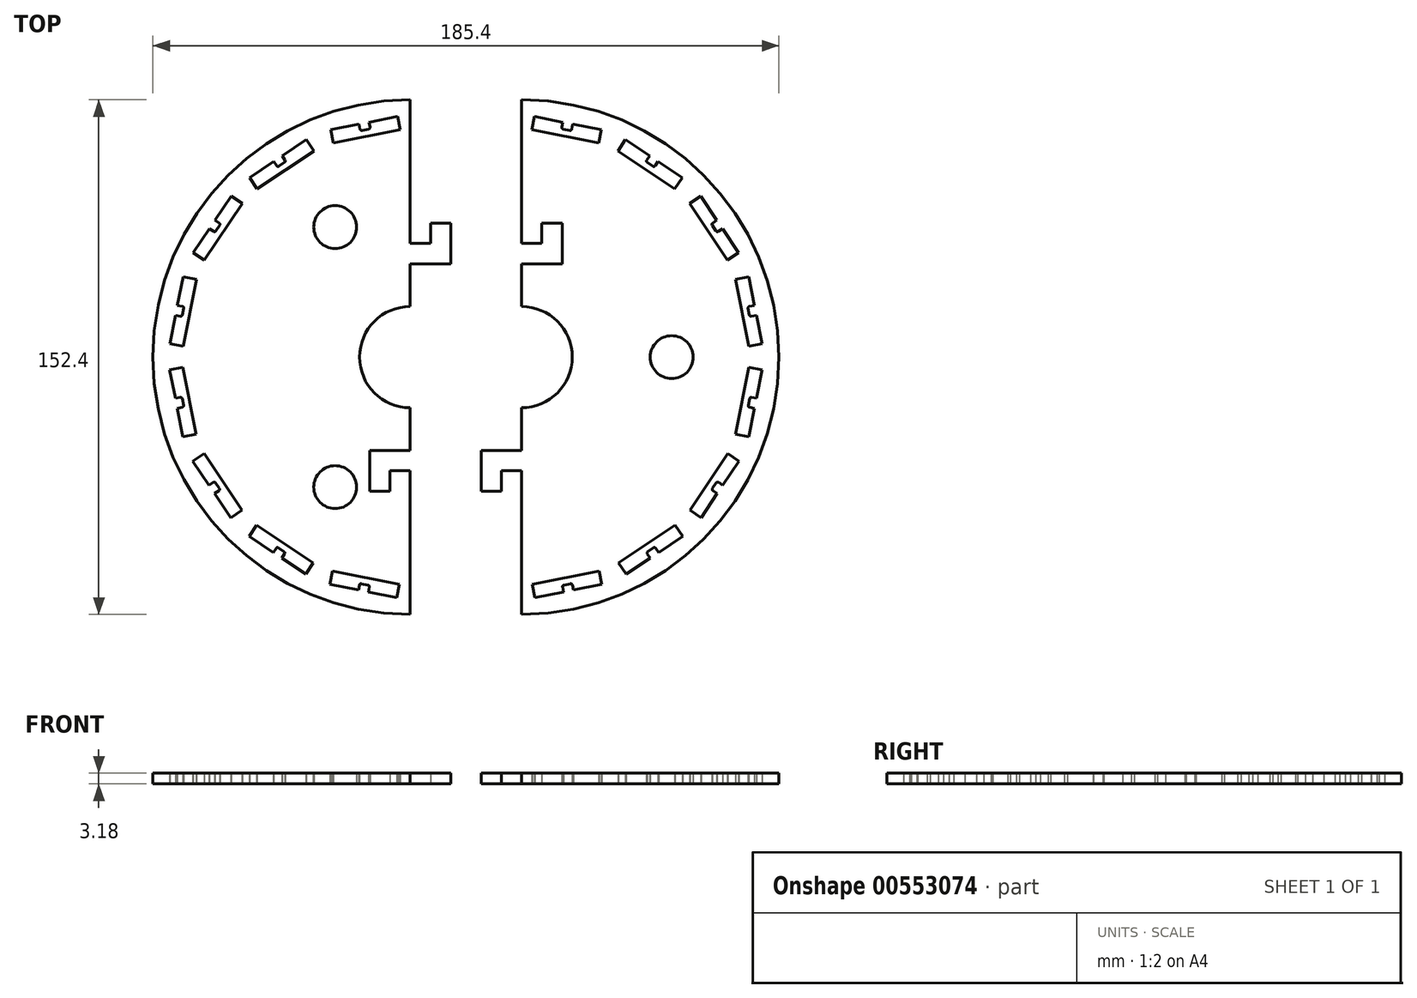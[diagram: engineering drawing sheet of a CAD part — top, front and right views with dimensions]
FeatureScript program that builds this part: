
annotation { "Feature Type Name" : "Feature", "Feature Type Description" : "" }
export const myFeature = defineFeature(function(context is Context, id is Id, definition is map)
    precondition{}
    {
        {
            var Q0;
            Q0=qCreatedBy(makeId("Top.planeOp"),FACE);
            var sketch = newSketch(context, id + "F0", { "sketchPlane" : qUnion([Q0])});
            skLineSegment(sketch, "E0.8.0", {"start": v(23, -63.34) * mm, "end": v(23.78, -67.27) * mm});
            skPoint(sketch, "E0.8.1", {"position": v(14.95, -66.98) * mm});
            skPoint(sketch, "E0.8.2", {"position": v(12.01, -67.57) * mm});
            skLineSegment(sketch, "E0.8.3", {"start": v(23, -63.34) * mm, "end": v(3.19, -67.28) * mm});
            skLineSegment(sketch, "E0.8.4", {"start": v(3.97, -71.2) * mm, "end": v(3.19, -67.28) * mm});
            skLineSegment(sketch, "E0.8.5", {"start": v(12.4, -69.53) * mm, "end": v(3.97, -71.2) * mm});
            skLineSegment(sketch, "E0.8.6", {"start": v(23.78, -67.27) * mm, "end": v(15.34, -68.94) * mm});
            skLineSegment(sketch, "E0.8.7", {"start": v(12.1, -68.06) * mm, "end": v(12.4, -69.53) * mm});
            skArc(sketch, "E0.8.8", {"start": v(15.05, -67.47) * mm, "mid": v(14.84, -67.15) * mm, "end": v(14.46, -67.08) * mm});
            skLineSegment(sketch, "E0.8.9", {"start": v(15.05, -67.47) * mm, "end": v(15.34, -68.94) * mm});
            skArc(sketch, "E0.8.10", {"start": v(12.5, -67.47) * mm, "mid": v(12.18, -67.68) * mm, "end": v(12.1, -68.06) * mm});
            skLineSegment(sketch, "E0.8.11", {"start": v(14.46, -67.08) * mm, "end": v(12.5, -67.47) * mm});
            skLineSegment(sketch, "E0.9.0", {"start": v(45.48, -49.72) * mm, "end": v(47.7, -53.05) * mm});
            skPoint(sketch, "E0.9.1", {"position": v(39.45, -56.16) * mm});
            skPoint(sketch, "E0.9.2", {"position": v(36.95, -57.83) * mm});
            skLineSegment(sketch, "E0.9.3", {"start": v(45.48, -49.72) * mm, "end": v(28.7, -60.94) * mm});
            skLineSegment(sketch, "E0.9.4", {"start": v(30.92, -64.27) * mm, "end": v(28.7, -60.94) * mm});
            skLineSegment(sketch, "E0.9.5", {"start": v(38.06, -59.5) * mm, "end": v(30.92, -64.27) * mm});
            skLineSegment(sketch, "E0.9.6", {"start": v(47.7, -53.05) * mm, "end": v(40.56, -57.82) * mm});
            skLineSegment(sketch, "E0.9.7", {"start": v(37.23, -58.24) * mm, "end": v(38.06, -59.5) * mm});
            skArc(sketch, "E0.9.8", {"start": v(39.73, -56.58) * mm, "mid": v(39.4, -56.36) * mm, "end": v(39.03, -56.44) * mm});
            skLineSegment(sketch, "E0.9.9", {"start": v(39.73, -56.58) * mm, "end": v(40.56, -57.82) * mm});
            skArc(sketch, "E0.9.10", {"start": v(37.37, -57.55) * mm, "mid": v(37.16, -57.87) * mm, "end": v(37.23, -58.24) * mm});
            skLineSegment(sketch, "E0.9.11", {"start": v(39.03, -56.44) * mm, "end": v(37.37, -57.55) * mm});
            skLineSegment(sketch, "E0.10.0", {"start": v(61.05, -28.53) * mm, "end": v(64.38, -30.75) * mm});
            skPoint(sketch, "E0.10.1", {"position": v(57.94, -36.8) * mm});
            skPoint(sketch, "E0.10.2", {"position": v(56.27, -39.28) * mm});
            skLineSegment(sketch, "E0.10.3", {"start": v(61.05, -28.53) * mm, "end": v(49.83, -45.32) * mm});
            skLineSegment(sketch, "E0.10.4", {"start": v(53.16, -47.54) * mm, "end": v(49.83, -45.32) * mm});
            skLineSegment(sketch, "E0.10.5", {"start": v(57.93, -40.4) * mm, "end": v(53.16, -47.54) * mm});
            skLineSegment(sketch, "E0.10.6", {"start": v(64.38, -30.75) * mm, "end": v(59.6, -37.9) * mm});
            skLineSegment(sketch, "E0.10.7", {"start": v(56.69, -39.56) * mm, "end": v(57.93, -40.4) * mm});
            skArc(sketch, "E0.10.8", {"start": v(58.35, -37.07) * mm, "mid": v(57.98, -37) * mm, "end": v(57.66, -37.2) * mm});
            skLineSegment(sketch, "E0.10.9", {"start": v(58.35, -37.07) * mm, "end": v(59.6, -37.9) * mm});
            skArc(sketch, "E0.10.10", {"start": v(56.55, -38.87) * mm, "mid": v(56.47, -39.24) * mm, "end": v(56.69, -39.56) * mm});
            skLineSegment(sketch, "E0.10.11", {"start": v(57.66, -37.2) * mm, "end": v(56.55, -38.87) * mm});
            skLineSegment(sketch, "E0.11.0", {"start": v(67.32, -3) * mm, "end": v(71.24, -3.78) * mm});
            skPoint(sketch, "E0.11.1", {"position": v(67.6, -11.82) * mm});
            skPoint(sketch, "E0.11.2", {"position": v(67.02, -14.76) * mm});
            skLineSegment(sketch, "E0.11.3", {"start": v(67.32, -3) * mm, "end": v(63.38, -22.8) * mm});
            skLineSegment(sketch, "E0.11.4", {"start": v(67.3, -23.58) * mm, "end": v(63.38, -22.8) * mm});
            skLineSegment(sketch, "E0.11.5", {"start": v(68.98, -15.15) * mm, "end": v(67.3, -23.58) * mm});
            skLineSegment(sketch, "E0.11.6", {"start": v(71.24, -3.78) * mm, "end": v(69.57, -12.2) * mm});
            skLineSegment(sketch, "E0.11.7", {"start": v(67.51, -14.86) * mm, "end": v(68.98, -15.15) * mm});
            skArc(sketch, "E0.11.8", {"start": v(68.1, -11.92) * mm, "mid": v(67.72, -12) * mm, "end": v(67.5, -12.3) * mm});
            skLineSegment(sketch, "E0.11.9", {"start": v(68.1, -11.92) * mm, "end": v(69.57, -12.2) * mm});
            skArc(sketch, "E0.11.10", {"start": v(67.12, -14.27) * mm, "mid": v(67.2, -14.65) * mm, "end": v(67.51, -14.86) * mm});
            skLineSegment(sketch, "E0.11.11", {"start": v(67.5, -12.3) * mm, "end": v(67.12, -14.27) * mm});
            skLineSegment(sketch, "E0.12.0", {"start": v(63.34, 23) * mm, "end": v(67.27, 23.78) * mm});
            skPoint(sketch, "E0.12.1", {"position": v(66.98, 14.95) * mm});
            skPoint(sketch, "E0.12.2", {"position": v(67.57, 12.01) * mm});
            skLineSegment(sketch, "E0.12.3", {"start": v(63.34, 23) * mm, "end": v(67.28, 3.19) * mm});
            skLineSegment(sketch, "E0.12.4", {"start": v(71.2, 3.97) * mm, "end": v(67.28, 3.19) * mm});
            skLineSegment(sketch, "E0.12.5", {"start": v(69.53, 12.4) * mm, "end": v(71.2, 3.97) * mm});
            skLineSegment(sketch, "E0.12.6", {"start": v(67.27, 23.78) * mm, "end": v(68.94, 15.34) * mm});
            skLineSegment(sketch, "E0.12.7", {"start": v(68.06, 12.1) * mm, "end": v(69.53, 12.4) * mm});
            skArc(sketch, "E0.12.8", {"start": v(67.47, 15.05) * mm, "mid": v(67.15, 14.84) * mm, "end": v(67.08, 14.46) * mm});
            skLineSegment(sketch, "E0.12.9", {"start": v(67.47, 15.05) * mm, "end": v(68.94, 15.34) * mm});
            skArc(sketch, "E0.12.10", {"start": v(67.47, 12.5) * mm, "mid": v(67.68, 12.18) * mm, "end": v(68.06, 12.1) * mm});
            skLineSegment(sketch, "E0.12.11", {"start": v(67.08, 14.46) * mm, "end": v(67.47, 12.5) * mm});
            skLineSegment(sketch, "E0.13.0", {"start": v(49.72, 45.48) * mm, "end": v(53.05, 47.7) * mm});
            skPoint(sketch, "E0.13.1", {"position": v(56.16, 39.45) * mm});
            skPoint(sketch, "E0.13.2", {"position": v(57.83, 36.95) * mm});
            skLineSegment(sketch, "E0.13.3", {"start": v(49.72, 45.48) * mm, "end": v(60.94, 28.7) * mm});
            skLineSegment(sketch, "E0.13.4", {"start": v(64.27, 30.92) * mm, "end": v(60.94, 28.7) * mm});
            skLineSegment(sketch, "E0.13.5", {"start": v(59.5, 38.06) * mm, "end": v(64.27, 30.92) * mm});
            skLineSegment(sketch, "E0.13.6", {"start": v(53.05, 47.7) * mm, "end": v(57.82, 40.56) * mm});
            skLineSegment(sketch, "E0.13.7", {"start": v(58.24, 37.23) * mm, "end": v(59.5, 38.06) * mm});
            skArc(sketch, "E0.13.8", {"start": v(56.58, 39.73) * mm, "mid": v(56.36, 39.4) * mm, "end": v(56.44, 39.03) * mm});
            skLineSegment(sketch, "E0.13.9", {"start": v(56.58, 39.73) * mm, "end": v(57.82, 40.56) * mm});
            skArc(sketch, "E0.13.10", {"start": v(57.55, 37.37) * mm, "mid": v(57.87, 37.16) * mm, "end": v(58.24, 37.23) * mm});
            skLineSegment(sketch, "E0.13.11", {"start": v(56.44, 39.03) * mm, "end": v(57.55, 37.37) * mm});
            skLineSegment(sketch, "E0.14.0", {"start": v(28.53, 61.05) * mm, "end": v(30.75, 64.38) * mm});
            skPoint(sketch, "E0.14.1", {"position": v(36.8, 57.94) * mm});
            skPoint(sketch, "E0.14.2", {"position": v(39.28, 56.27) * mm});
            skLineSegment(sketch, "E0.14.3", {"start": v(28.53, 61.05) * mm, "end": v(45.32, 49.83) * mm});
            skLineSegment(sketch, "E0.14.4", {"start": v(47.54, 53.16) * mm, "end": v(45.32, 49.83) * mm});
            skLineSegment(sketch, "E0.14.5", {"start": v(40.4, 57.93) * mm, "end": v(47.54, 53.16) * mm});
            skLineSegment(sketch, "E0.14.6", {"start": v(30.75, 64.38) * mm, "end": v(37.9, 59.6) * mm});
            skLineSegment(sketch, "E0.14.7", {"start": v(39.56, 56.69) * mm, "end": v(40.4, 57.93) * mm});
            skArc(sketch, "E0.14.8", {"start": v(37.07, 58.35) * mm, "mid": v(37, 57.98) * mm, "end": v(37.2, 57.66) * mm});
            skLineSegment(sketch, "E0.14.9", {"start": v(37.07, 58.35) * mm, "end": v(37.9, 59.6) * mm});
            skArc(sketch, "E0.14.10", {"start": v(38.87, 56.55) * mm, "mid": v(39.24, 56.47) * mm, "end": v(39.56, 56.69) * mm});
            skLineSegment(sketch, "E0.14.11", {"start": v(37.2, 57.66) * mm, "end": v(38.87, 56.55) * mm});
            skLineSegment(sketch, "E0.15.0", {"start": v(3, 67.32) * mm, "end": v(3.78, 71.24) * mm});
            skPoint(sketch, "E0.15.1", {"position": v(11.82, 67.6) * mm});
            skPoint(sketch, "E0.15.2", {"position": v(14.76, 67.02) * mm});
            skLineSegment(sketch, "E0.15.3", {"start": v(3, 67.32) * mm, "end": v(22.8, 63.38) * mm});
            skLineSegment(sketch, "E0.15.4", {"start": v(23.58, 67.3) * mm, "end": v(22.8, 63.38) * mm});
            skLineSegment(sketch, "E0.15.5", {"start": v(15.15, 68.98) * mm, "end": v(23.58, 67.3) * mm});
            skLineSegment(sketch, "E0.15.6", {"start": v(3.78, 71.24) * mm, "end": v(12.2, 69.57) * mm});
            skLineSegment(sketch, "E0.15.7", {"start": v(14.86, 67.51) * mm, "end": v(15.15, 68.98) * mm});
            skArc(sketch, "E0.15.8", {"start": v(11.92, 68.1) * mm, "mid": v(12, 67.72) * mm, "end": v(12.3, 67.5) * mm});
            skLineSegment(sketch, "E0.15.9", {"start": v(11.92, 68.1) * mm, "end": v(12.2, 69.57) * mm});
            skArc(sketch, "E0.15.10", {"start": v(14.27, 67.12) * mm, "mid": v(14.65, 67.2) * mm, "end": v(14.86, 67.51) * mm});
            skLineSegment(sketch, "E0.15.11", {"start": v(12.3, 67.5) * mm, "end": v(14.27, 67.12) * mm});
            skPoint(sketch, "E0.center", {"position": v(0, 0) * mm});
            skArc(sketch, "E1", {"start": v(0, -76.2) * mm, "mid": v(76.2, 0) * mm, "end": v(0, 76.2) * mm});
            skArc(sketch, "E2", {"start": v(0, -15) * mm, "mid": v(15, 0) * mm, "end": v(0, 15) * mm});
            skLineSegment(sketch, "E3", {"start": v(0, 33.66) * mm, "end": v(6, 33.66) * mm});
            skLineSegment(sketch, "E4", {"start": v(6, 33.66) * mm, "end": v(6, 39.66) * mm});
            skLineSegment(sketch, "E5", {"start": v(6, 39.66) * mm, "end": v(12, 39.66) * mm});
            skLineSegment(sketch, "E6", {"start": v(12, 39.66) * mm, "end": v(12, 27.66) * mm});
            skLineSegment(sketch, "E7", {"start": v(12, 27.66) * mm, "end": v(0, 27.66) * mm});
            skLineSegment(sketch, "E8.1.0", {"start": v(-12, -27.66) * mm, "end": v(0, -27.66) * mm});
            skLineSegment(sketch, "E8.1.1", {"start": v(-6, -39.66) * mm, "end": v(-12, -39.66) * mm});
            skLineSegment(sketch, "E8.1.2", {"start": v(0, -33.66) * mm, "end": v(-6, -33.66) * mm});
            skLineSegment(sketch, "E8.1.3", {"start": v(-6, -33.66) * mm, "end": v(-6, -39.66) * mm});
            skLineSegment(sketch, "E8.1.4", {"start": v(-12, -39.66) * mm, "end": v(-12, -27.66) * mm});
            skLineSegment(sketch, "E9", {"start": v(0, -27.66) * mm, "end": v(0, -15) * mm});
            skLineSegment(sketch, "E10", {"start": v(0, 15) * mm, "end": v(0, 27.66) * mm});
            skLineSegment(sketch, "E11", {"start": v(0, 33.66) * mm, "end": v(0, 76.2) * mm});
            skLineSegment(sketch, "E12", {"start": v(0, -33.66) * mm, "end": v(0, -76.2) * mm});
            skPoint(sketch, "E13.center", {"position": v(-33, 0) * mm});
            skLineSegment(sketch, "E14", {"start": v(-33, 33.66) * mm, "end": v(-27, 33.66) * mm});
            skLineSegment(sketch, "E15", {"start": v(-27, 33.66) * mm, "end": v(-27, 39.66) * mm});
            skLineSegment(sketch, "E16", {"start": v(-27, 39.66) * mm, "end": v(-21, 39.66) * mm});
            skLineSegment(sketch, "E17", {"start": v(-21, 39.66) * mm, "end": v(-21, 27.66) * mm});
            skLineSegment(sketch, "E18", {"start": v(-21, 27.66) * mm, "end": v(-33, 27.66) * mm});
            skLineSegment(sketch, "E19.1.0", {"start": v(-45, -27.66) * mm, "end": v(-33, -27.66) * mm});
            skLineSegment(sketch, "E19.1.1", {"start": v(-39, -39.66) * mm, "end": v(-45, -39.66) * mm});
            skLineSegment(sketch, "E19.1.2", {"start": v(-33, -33.66) * mm, "end": v(-39, -33.66) * mm});
            skLineSegment(sketch, "E19.1.3", {"start": v(-39, -33.66) * mm, "end": v(-39, -39.66) * mm});
            skLineSegment(sketch, "E19.1.4", {"start": v(-45, -39.66) * mm, "end": v(-45, -27.66) * mm});
            skLineSegment(sketch, "E20", {"start": v(-33, -27.66) * mm, "end": v(-33, -15) * mm});
            skLineSegment(sketch, "E21", {"start": v(-33, 15) * mm, "end": v(-33, 27.66) * mm});
            skLineSegment(sketch, "E22", {"start": v(-33, 33.66) * mm, "end": v(-33, 76.2) * mm});
            skLineSegment(sketch, "E23", {"start": v(-33, -33.66) * mm, "end": v(-33, -76.2) * mm});
            skArc(sketch, "E24.MirrorCS", {"start": v(-100.47, 15.05) * mm, "mid": v(-100.15, 14.84) * mm, "end": v(-100.08, 14.46) * mm});
            skArc(sketch, "E25.MirrorCS", {"start": v(-48.05, -67.47) * mm, "mid": v(-47.84, -67.15) * mm, "end": v(-47.46, -67.08) * mm});
            skArc(sketch, "E26.MirrorCS", {"start": v(-101.1, -11.92) * mm, "mid": v(-100.72, -12) * mm, "end": v(-100.5, -12.3) * mm});
            skArc(sketch, "E27.MirrorCS", {"start": v(-45.5, -67.47) * mm, "mid": v(-45.18, -67.68) * mm, "end": v(-45.1, -68.06) * mm});
            skArc(sketch, "E28.MirrorCS", {"start": v(-100.47, 12.5) * mm, "mid": v(-100.68, 12.18) * mm, "end": v(-101.06, 12.1) * mm});
            skLineSegment(sketch, "E29.MirrorCS", {"start": v(-47.86, 67.51) * mm, "end": v(-48.15, 68.98) * mm});
            skArc(sketch, "E30.MirrorCS", {"start": v(-44.92, 68.1) * mm, "mid": v(-45, 67.72) * mm, "end": v(-45.3, 67.5) * mm});
            skLineSegment(sketch, "E31.MirrorCS", {"start": v(-48.05, -67.47) * mm, "end": v(-48.34, -68.94) * mm});
            skLineSegment(sketch, "E32.MirrorCS", {"start": v(-45.3, 67.5) * mm, "end": v(-47.27, 67.12) * mm});
            skLineSegment(sketch, "E33.MirrorCS", {"start": v(-100.47, 15.05) * mm, "end": v(-101.94, 15.34) * mm});
            skLineSegment(sketch, "E34.MirrorCS", {"start": v(-44.92, 68.1) * mm, "end": v(-45.2, 69.57) * mm});
            skArc(sketch, "E35.MirrorCS", {"start": v(-91.35, -37.07) * mm, "mid": v(-90.98, -37) * mm, "end": v(-90.66, -37.2) * mm});
            skArc(sketch, "E36.MirrorCS", {"start": v(-71.87, 56.55) * mm, "mid": v(-72.24, 56.47) * mm, "end": v(-72.56, 56.69) * mm});
            skLineSegment(sketch, "E37.MirrorCS", {"start": v(-101.06, 12.1) * mm, "end": v(-102.53, 12.4) * mm});
            skArc(sketch, "E38.MirrorCS", {"start": v(-100.12, -14.27) * mm, "mid": v(-100.2, -14.65) * mm, "end": v(-100.51, -14.86) * mm});
            skArc(sketch, "E39.MirrorCS", {"start": v(-47.27, 67.12) * mm, "mid": v(-47.65, 67.2) * mm, "end": v(-47.86, 67.51) * mm});
            skLineSegment(sketch, "E40.MirrorCS", {"start": v(-70.23, -58.24) * mm, "end": v(-71.06, -59.5) * mm});
            skLineSegment(sketch, "E41.MirrorCS", {"start": v(-100.51, -14.86) * mm, "end": v(-101.98, -15.15) * mm});
            skLineSegment(sketch, "E42.MirrorCS", {"start": v(-100.08, 14.46) * mm, "end": v(-100.47, 12.5) * mm});
            skLineSegment(sketch, "E43.MirrorCS", {"start": v(-101.1, -11.92) * mm, "end": v(-102.57, -12.2) * mm});
            skLineSegment(sketch, "E44.MirrorCS", {"start": v(-100.5, -12.3) * mm, "end": v(-100.12, -14.27) * mm});
            skLineSegment(sketch, "E45.MirrorCS", {"start": v(-47.46, -67.08) * mm, "end": v(-45.5, -67.47) * mm});
            skArc(sketch, "E46.MirrorCS", {"start": v(-89.55, -38.87) * mm, "mid": v(-89.47, -39.24) * mm, "end": v(-89.69, -39.56) * mm});
            skLineSegment(sketch, "E47.MirrorCS", {"start": v(-45.1, -68.06) * mm, "end": v(-45.4, -69.53) * mm});
            skLineSegment(sketch, "E48.MirrorCS", {"start": v(-70.07, 58.35) * mm, "end": v(-70.9, 59.6) * mm});
            skLineSegment(sketch, "E49.MirrorCS", {"start": v(-72.03, -56.44) * mm, "end": v(-70.37, -57.55) * mm});
            skArc(sketch, "E50.MirrorCS", {"start": v(-72.73, -56.58) * mm, "mid": v(-72.4, -56.36) * mm, "end": v(-72.03, -56.44) * mm});
            skArc(sketch, "E51.MirrorCS", {"start": v(-70.37, -57.55) * mm, "mid": v(-70.16, -57.87) * mm, "end": v(-70.23, -58.24) * mm});
            skLineSegment(sketch, "E52.MirrorCS", {"start": v(-89.69, -39.56) * mm, "end": v(-90.93, -40.4) * mm});
            skLineSegment(sketch, "E53.MirrorCS", {"start": v(-70.2, 57.66) * mm, "end": v(-71.87, 56.55) * mm});
            skArc(sketch, "E54.MirrorCS", {"start": v(-89.58, 39.73) * mm, "mid": v(-89.36, 39.4) * mm, "end": v(-89.44, 39.03) * mm});
            skLineSegment(sketch, "E55.MirrorCS", {"start": v(-90.66, -37.2) * mm, "end": v(-89.55, -38.87) * mm});
            skLineSegment(sketch, "E56.MirrorCS", {"start": v(-72.56, 56.69) * mm, "end": v(-73.4, 57.93) * mm});
            skLineSegment(sketch, "E57.MirrorCS", {"start": v(-91.35, -37.07) * mm, "end": v(-92.6, -37.9) * mm});
            skLineSegment(sketch, "E58.MirrorCS", {"start": v(-72.73, -56.58) * mm, "end": v(-73.56, -57.82) * mm});
            skArc(sketch, "E59.MirrorCS", {"start": v(-90.55, 37.37) * mm, "mid": v(-90.87, 37.16) * mm, "end": v(-91.24, 37.23) * mm});
            skArc(sketch, "E60.MirrorCS", {"start": v(-70.07, 58.35) * mm, "mid": v(-70, 57.98) * mm, "end": v(-70.2, 57.66) * mm});
            skLineSegment(sketch, "E61.MirrorCS", {"start": v(-89.44, 39.03) * mm, "end": v(-90.55, 37.37) * mm});
            skLineSegment(sketch, "E62.MirrorCS", {"start": v(-91.24, 37.23) * mm, "end": v(-92.5, 38.06) * mm});
            skLineSegment(sketch, "E63.MirrorCS", {"start": v(-89.58, 39.73) * mm, "end": v(-90.82, 40.56) * mm});
            skLineSegment(sketch, "E64.MirrorCS", {"start": v(-100.32, -3) * mm, "end": v(-96.38, -22.8) * mm});
            skLineSegment(sketch, "E65.MirrorCS", {"start": v(-45.4, -69.53) * mm, "end": v(-36.97, -71.2) * mm});
            skLineSegment(sketch, "E66.MirrorCS", {"start": v(-56.58, 67.3) * mm, "end": v(-55.8, 63.38) * mm});
            skLineSegment(sketch, "E67.MirrorCS", {"start": v(-100.32, -3) * mm, "end": v(-104.24, -3.78) * mm});
            skLineSegment(sketch, "E68.MirrorCS", {"start": v(-36, 67.32) * mm, "end": v(-55.8, 63.38) * mm});
            skLineSegment(sketch, "E69.MirrorCS", {"start": v(-86.05, 47.7) * mm, "end": v(-90.82, 40.56) * mm});
            skLineSegment(sketch, "E70.MirrorCS", {"start": v(-78.48, -49.72) * mm, "end": v(-80.7, -53.05) * mm});
            skLineSegment(sketch, "E71.MirrorCS", {"start": v(-36, 67.32) * mm, "end": v(-36.78, 71.24) * mm});
            skLineSegment(sketch, "E72.MirrorCS", {"start": v(-73.4, 57.93) * mm, "end": v(-80.54, 53.16) * mm});
            skLineSegment(sketch, "E73.MirrorCS", {"start": v(-56, -63.34) * mm, "end": v(-56.78, -67.27) * mm});
            skLineSegment(sketch, "E74.MirrorCS", {"start": v(-61.53, 61.05) * mm, "end": v(-78.32, 49.83) * mm});
            skLineSegment(sketch, "E75.MirrorCS", {"start": v(-104.2, 3.97) * mm, "end": v(-100.28, 3.19) * mm});
            skLineSegment(sketch, "E76.MirrorCS", {"start": v(-56, -63.34) * mm, "end": v(-36.19, -67.28) * mm});
            skLineSegment(sketch, "E77.MirrorCS", {"start": v(-56.78, -67.27) * mm, "end": v(-48.34, -68.94) * mm});
            skLineSegment(sketch, "E78.MirrorCS", {"start": v(-92.5, 38.06) * mm, "end": v(-97.27, 30.92) * mm});
            skLineSegment(sketch, "E79.MirrorCS", {"start": v(-36.97, -71.2) * mm, "end": v(-36.19, -67.28) * mm});
            skLineSegment(sketch, "E80.MirrorCS", {"start": v(-96.34, 23) * mm, "end": v(-100.28, 3.19) * mm});
            skLineSegment(sketch, "E81.MirrorCS", {"start": v(-104.24, -3.78) * mm, "end": v(-102.57, -12.2) * mm});
            skLineSegment(sketch, "E82.MirrorCS", {"start": v(-90.93, -40.4) * mm, "end": v(-86.16, -47.54) * mm});
            skLineSegment(sketch, "E83.MirrorCS", {"start": v(-94.05, -28.53) * mm, "end": v(-82.83, -45.32) * mm});
            skLineSegment(sketch, "E84.MirrorCS", {"start": v(-63.92, -64.27) * mm, "end": v(-61.7, -60.94) * mm});
            skLineSegment(sketch, "E85.MirrorCS", {"start": v(-78.48, -49.72) * mm, "end": v(-61.7, -60.94) * mm});
            skLineSegment(sketch, "E86.MirrorCS", {"start": v(-94.05, -28.53) * mm, "end": v(-97.38, -30.75) * mm});
            skLineSegment(sketch, "E87.MirrorCS", {"start": v(-97.27, 30.92) * mm, "end": v(-93.94, 28.7) * mm});
            skLineSegment(sketch, "E88.MirrorCS", {"start": v(-102.53, 12.4) * mm, "end": v(-104.2, 3.97) * mm});
            skLineSegment(sketch, "E89.MirrorCS", {"start": v(-61.53, 61.05) * mm, "end": v(-63.75, 64.38) * mm});
            skLineSegment(sketch, "E90.MirrorCS", {"start": v(-63.75, 64.38) * mm, "end": v(-70.9, 59.6) * mm});
            skLineSegment(sketch, "E91.MirrorCS", {"start": v(-100.27, 23.78) * mm, "end": v(-101.94, 15.34) * mm});
            skLineSegment(sketch, "E92.MirrorCS", {"start": v(-82.72, 45.48) * mm, "end": v(-93.94, 28.7) * mm});
            skLineSegment(sketch, "E93.MirrorCS", {"start": v(-48.15, 68.98) * mm, "end": v(-56.58, 67.3) * mm});
            skLineSegment(sketch, "E94.MirrorCS", {"start": v(-97.38, -30.75) * mm, "end": v(-92.6, -37.9) * mm});
            skLineSegment(sketch, "E95.MirrorCS", {"start": v(-80.7, -53.05) * mm, "end": v(-73.56, -57.82) * mm});
            skLineSegment(sketch, "E96.MirrorCS", {"start": v(-100.3, -23.58) * mm, "end": v(-96.38, -22.8) * mm});
            skLineSegment(sketch, "E97.MirrorCS", {"start": v(-101.98, -15.15) * mm, "end": v(-100.3, -23.58) * mm});
            skLineSegment(sketch, "E98.MirrorCS", {"start": v(-96.34, 23) * mm, "end": v(-100.27, 23.78) * mm});
            skLineSegment(sketch, "E99.MirrorCS", {"start": v(-36.78, 71.24) * mm, "end": v(-45.2, 69.57) * mm});
            skLineSegment(sketch, "E100.MirrorCS", {"start": v(-82.72, 45.48) * mm, "end": v(-86.05, 47.7) * mm});
            skLineSegment(sketch, "E101.MirrorCS", {"start": v(-86.16, -47.54) * mm, "end": v(-82.83, -45.32) * mm});
            skLineSegment(sketch, "E102.MirrorCS", {"start": v(-80.54, 53.16) * mm, "end": v(-78.32, 49.83) * mm});
            skLineSegment(sketch, "E103.MirrorCS", {"start": v(-71.06, -59.5) * mm, "end": v(-63.92, -64.27) * mm});
            skPoint(sketch, "E104.MirrorP", {"position": v(-44.82, 67.6) * mm});
            skPoint(sketch, "E105.MirrorP", {"position": v(-90.83, 36.95) * mm});
            skPoint(sketch, "E106.MirrorP", {"position": v(-45.01, -67.57) * mm});
            skPoint(sketch, "E107.MirrorP", {"position": v(-69.95, -57.83) * mm});
            skArc(sketch, "E108.MirrorCS", {"start": v(-33, -76.2) * mm, "mid": v(-109.2, 0) * mm, "end": v(-33, 76.2) * mm});
            skPoint(sketch, "E109.MirrorP", {"position": v(-100.6, -11.82) * mm});
            skPoint(sketch, "E110.MirrorP", {"position": v(-47.76, 67.02) * mm});
            skArc(sketch, "E111.MirrorCS", {"start": v(-33, -15) * mm, "mid": v(-48, 0) * mm, "end": v(-33, 15) * mm});
            skPoint(sketch, "E112.MirrorP", {"position": v(-72.45, -56.16) * mm});
            skPoint(sketch, "E113.MirrorP", {"position": v(-69.8, 57.94) * mm});
            skPoint(sketch, "E114.MirrorP", {"position": v(-47.95, -66.98) * mm});
            skPoint(sketch, "E115.MirrorP", {"position": v(-99.98, 14.95) * mm});
            skPoint(sketch, "E116.MirrorP", {"position": v(-72.28, 56.27) * mm});
            skPoint(sketch, "E117.MirrorP", {"position": v(-100.02, -14.76) * mm});
            skPoint(sketch, "E118.MirrorP", {"position": v(-89.27, -39.28) * mm});
            skPoint(sketch, "E119.MirrorP", {"position": v(-100.57, 12.01) * mm});
            skPoint(sketch, "E120.MirrorP", {"position": v(-90.94, -36.8) * mm});
            skPoint(sketch, "E121.MirrorP", {"position": v(-89.16, 39.45) * mm});
            skCircle(sketch, "E122", {"center": v(-55.23, 38.5) * mm, "radius": 6.35 * mm});
            skCircle(sketch, "E123.1.0", {"center": v(-55.23, -38.5) * mm, "radius": 6.35 * mm});
            skCircle(sketch, "E123.2.0", {"center": v(44.45, 0) * mm, "radius": 6.35 * mm});
            skSolve(sketch);
        }
        {
            var Q0;
            Q0=makeQuery(id+"F0.imprint","IMPRINT",FACE,{"disambiguationData":[TD([[makeQuery(id+"F0.imprint","IMPRINT",EDGE,{"derivedFrom":sQuery(id+"F0.wireOp",EDGE,"E0.8.0")}),1.0]])]});
            extrude(context, id + "F1", {"entities" : qUnion([Q0]), "depth" : 3.17 * mm, "offsetDistance" : 25 * mm});
        }
        {
            var Q0;
            Q0=makeQuery(id+"F0.imprint","IMPRINT",FACE,{"disambiguationData":[TD([[makeQuery(id+"F0.imprint","IMPRINT",EDGE,{"derivedFrom":sQuery(id+"F0.wireOp",EDGE,"E14")}),-1.0]])]});
            extrude(context, id + "F2", {"entities" : qUnion([Q0]), "depth" : 3.17 * mm, "offsetDistance" : 25 * mm});
        }
    });
